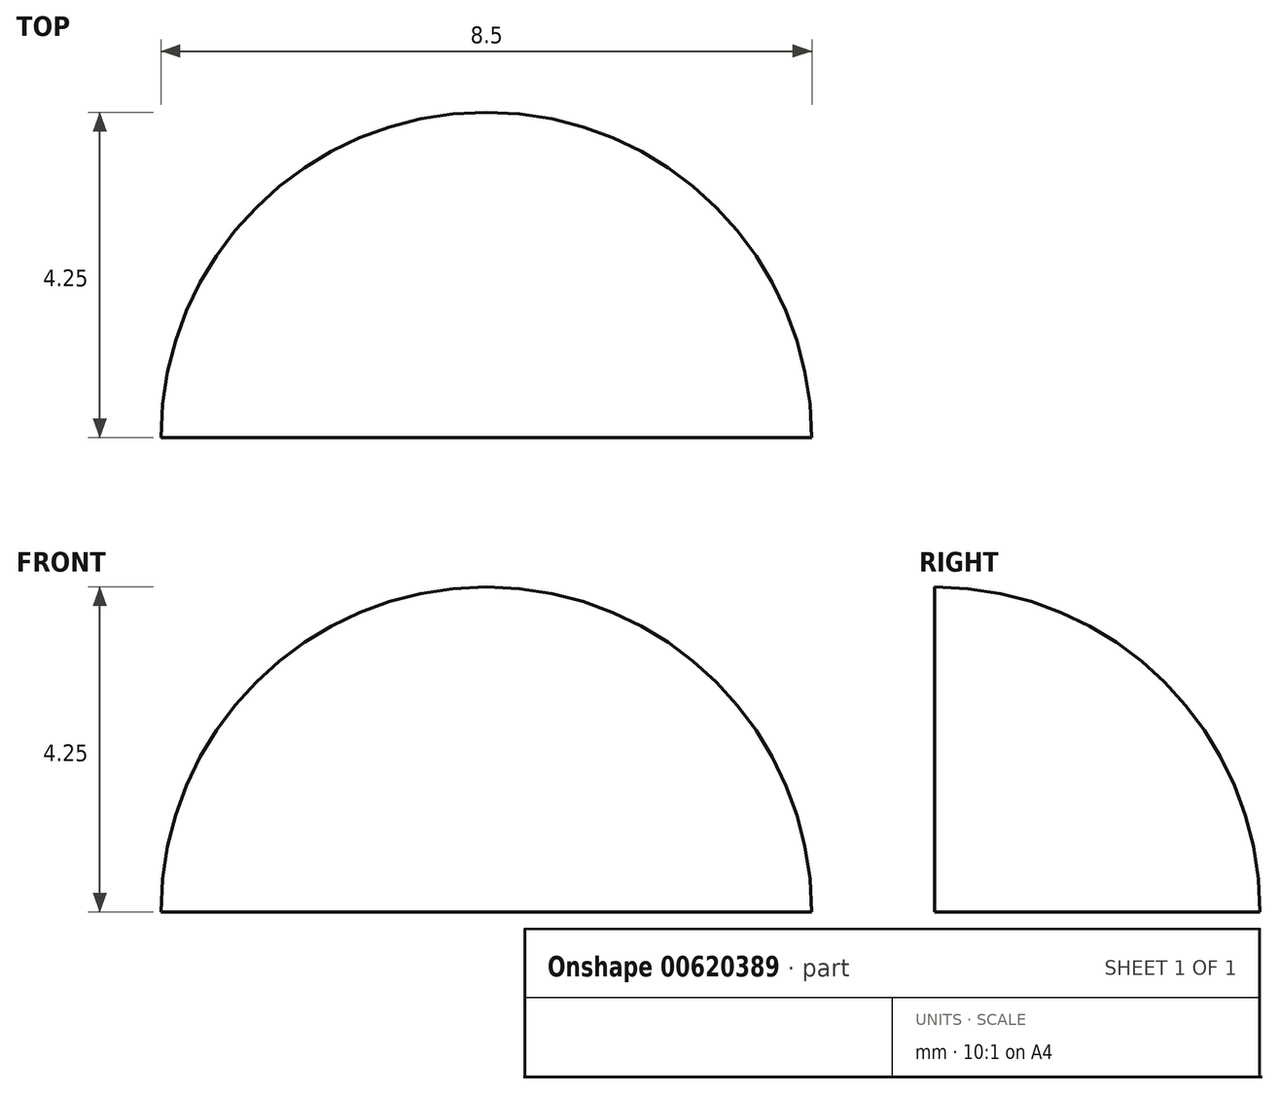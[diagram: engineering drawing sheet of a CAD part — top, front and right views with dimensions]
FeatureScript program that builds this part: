
annotation { "Feature Type Name" : "Feature", "Feature Type Description" : "" }
export const myFeature = defineFeature(function(context is Context, id is Id, definition is map)
    precondition{}
    {
        {
            var Q0;
            Q0=qCreatedBy(makeId("Top.planeOp"),FACE);
            var sketch = newSketch(context, id + "F0", { "sketchPlane" : qUnion([Q0])});
            skLineSegment(sketch, "E0", {"start": v(-45.77, -38.14) * mm, "end": v(-37.27, -38.14) * mm});
            skArc(sketch, "E1", {"start": v(-37.27, -38.14) * mm, "mid": v(-41.52, -33.89) * mm, "end": v(-45.77, -38.14) * mm});
            skPoint(sketch, "E2", {"position": v(-41.52, -33.89) * mm});
            skSolve(sketch);
        }
        {
            var Q0;
            Q0=makeQuery(id+"F0.imprint","IMPRINT",FACE,{"disambiguationData":[TD([[makeQuery(id+"F0.imprint","IMPRINT",EDGE,{"derivedFrom":sQuery(id+"F0.wireOp",EDGE,"E0")}),1.0]])]});
            var Q1;
            Q1=sQuery(id+"F0.wireOp",EDGE,"E0");
            revolve(context, id + "F1", {"entities" : qUnion([Q0]), "axis" : qUnion([Q1]), "revolveType" : RevolveType.ONE_DIRECTION, "angle" : 90 * degree});
        }
    });
